# Revit family: Energieverteiler UVS, mit Steckanschluss 5-polig, 6 Ausgangbuchen 3-polig
name_source: partatom
category: Generic Models
revit_build: Autodesk Revit 2015 (Build: 20140606_1530(x64)
units: mm (PartAtom-declared; Revit-internal decimal feet)

## types (4) — shared parameters
Height = 43 mm
Length = 150 mm
Length 1 = 135 mm  [stored 0.442913 ft]
Manufacturer = OBO Bettermann
Material 3 = Plastic Black
URL = http://www.obo-bettermann.com
Width = 160 mm  [stored 0.524934 ft]

## per-type parameters (varying)
| type | GTIN | Height 1 | Height 2 | Manufacturer Art.No. | Material | Material 2 | Width 1 | Width 2 |
| UVS-6S2SA | 4012195522997 | 10 mm  [stored 0.0328084 ft] | 18 mm  [stored 0.0590551 ft] | 6108012 | Steel | Plastic Black | 31 mm  [stored 0.101706 ft] | 53 mm  [stored 0.173885 ft] |
| UVS-6W2SA | 4012195523000 | 10 mm  [stored 0.0328084 ft] | 18 mm  [stored 0.0590551 ft] | 6108014 | Steel | Plastic White | 31 mm  [stored 0.101706 ft] | 53 mm  [stored 0.173885 ft] |
| UVS-6S2SA1P | 4012195685050 | 2 mm  [stored 0.00656168 ft] | 36 mm | 6108013 | Steel, Galvanized | Plastic Black | 43 mm | 18 mm  [stored 0.0590551 ft] |
| UVS-6W2SA1P | 4012195685067 | 2 mm  [stored 0.00656168 ft] | 36 mm | 6108015 | Steel, Galvanized | Plastic White | 43 mm | 18 mm  [stored 0.0590551 ft] |

note: column(s) folded — value = type name in every type: Article Type

note: [stored X ft] marks values corroborated as IEEE doubles in the binary element streams (Revit-internal decimal feet)

## geometry (parser evidence)
native form markers: Sweep x2
no freeform markers — native parametric forms only
